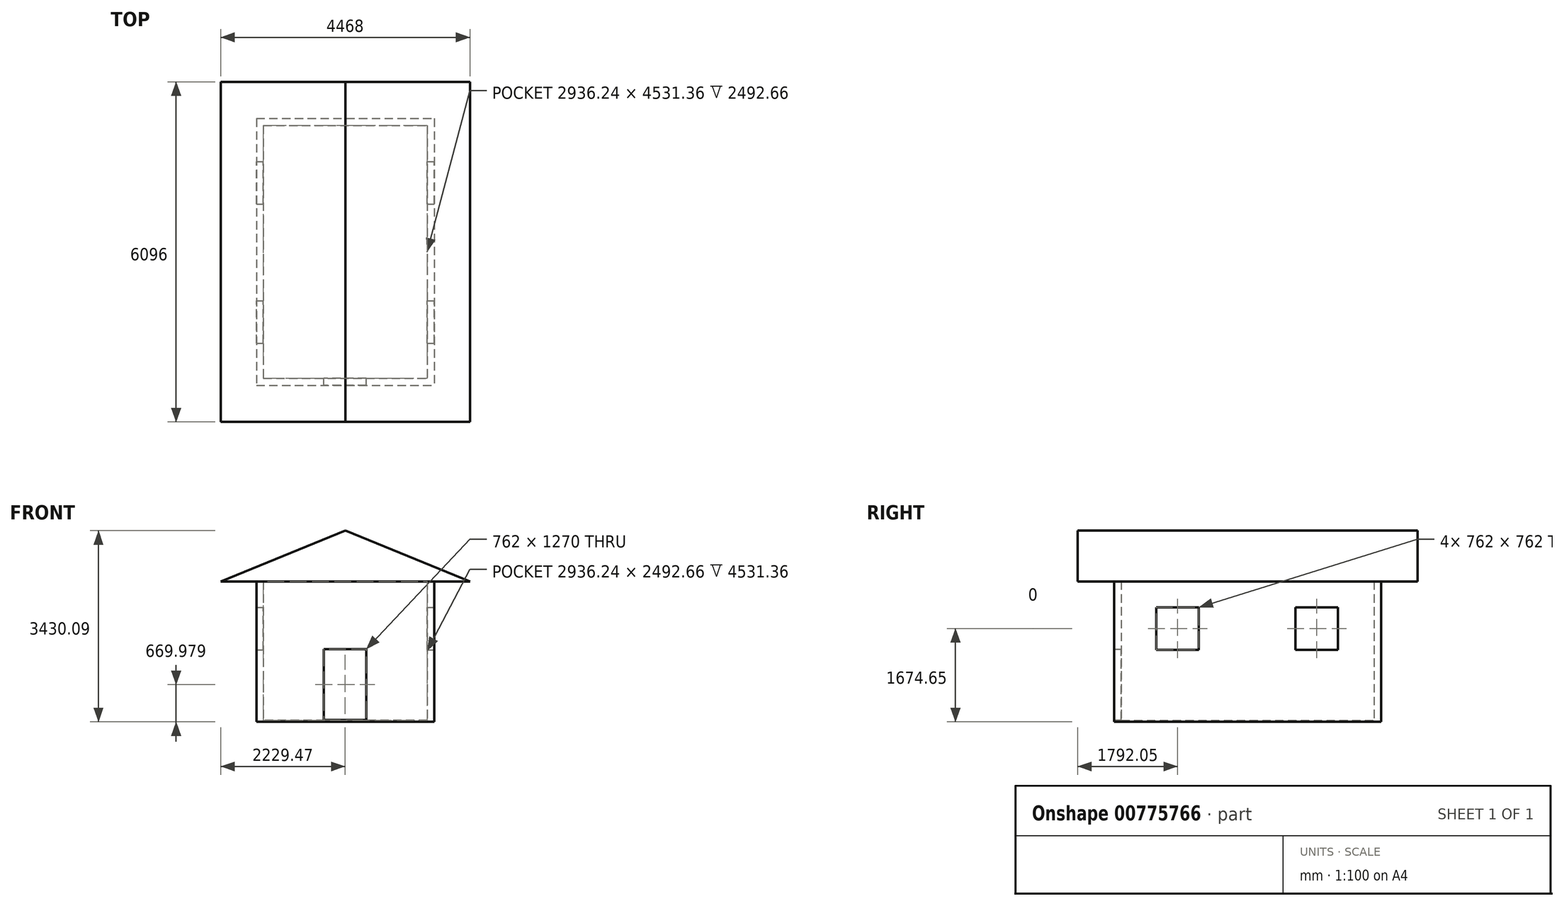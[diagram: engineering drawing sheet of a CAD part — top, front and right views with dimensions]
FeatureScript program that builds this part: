
annotation { "Feature Type Name" : "Feature", "Feature Type Description" : "" }
export const myFeature = defineFeature(function(context is Context, id is Id, definition is map)
    precondition{}
    {
        {
            var Q0;
            Q0=qCreatedBy(makeId("Top.planeOp"),FACE);
            var sketch = newSketch(context, id + "F0", { "sketchPlane" : qUnion([Q0])});
            skLineSegment(sketch, "E0.bottom", {"start": v(1595.12, -2392.68) * mm, "end": v(-1595.12, -2392.68) * mm});
            skLineSegment(sketch, "E0.top", {"start": v(1595.12, 2392.68) * mm, "end": v(-1595.12, 2392.68) * mm});
            skLineSegment(sketch, "E0.left", {"start": v(1595.12, -2392.68) * mm, "end": v(1595.12, 2392.68) * mm});
            skLineSegment(sketch, "E0.right", {"start": v(-1595.12, -2392.68) * mm, "end": v(-1595.12, 2392.68) * mm});
            skPoint(sketch, "E0.middle", {"position": v(0, 0) * mm});
            skLineSegment(sketch, "E1.bottom", {"start": v(1468.12, -2265.68) * mm, "end": v(-1468.12, -2265.68) * mm});
            skLineSegment(sketch, "E1.top", {"start": v(1468.12, 2265.68) * mm, "end": v(-1468.12, 2265.68) * mm});
            skLineSegment(sketch, "E1.left", {"start": v(1468.12, -2265.68) * mm, "end": v(1468.12, 2265.68) * mm});
            skLineSegment(sketch, "E1.right", {"start": v(-1468.12, -2265.68) * mm, "end": v(-1468.12, 2265.68) * mm});
            skSolve(sketch);
        }
        {
            var Q0;
            Q0=makeQuery(id+"F0.imprint","IMPRINT",FACE,{"disambiguationData":[TD([[makeQuery(id+"F0.imprint","IMPRINT",EDGE,{"derivedFrom":sQuery(id+"F0.wireOp",EDGE,"E0.bottom")}),-1.0]])]});
            extrude(context, id + "F1", {"entities" : qUnion([Q0]), "depth" : 2540 * mm, "offsetDistance" : 25.4 * mm});
        }
        {
            var Q0;
            Q0=makeQuery(id+"F0.imprint","IMPRINT",FACE,{"disambiguationData":[TD([[makeQuery(id+"F0.imprint","IMPRINT",EDGE,{"derivedFrom":sQuery(id+"F0.wireOp",EDGE,"E1.bottom")}),-1.0]])]});
            extrude(context, id + "F2", {"entities" : qUnion([Q0]), "operationType" : NewBodyOperationType.ADD, "depth" : 25.4 * mm, "offsetDistance" : 25.4 * mm});
        }
        {
            var Q0;
            Q0=qCreatedBy(makeId("Front.planeOp"),FACE);
            var sketch = newSketch(context, id + "F3", { "sketchPlane" : qUnion([Q0])});
            skLineSegment(sketch, "E2", {"start": v(-2234, 2518.06) * mm, "end": v(0, 3430.09) * mm});
            skLineSegment(sketch, "E3", {"start": v(0, 3430.09) * mm, "end": v(2234, 2518.06) * mm});
            skLineSegment(sketch, "E4", {"start": v(2234, 2518.06) * mm, "end": v(-2234, 2518.06) * mm});
            skSolve(sketch);
        }
        {
            var Q0;
            Q0 = qSketchRegion(id + "F3", true);
            extrude(context, id + "F4", {"entities" : qUnion([Q0]), "operationType" : NewBodyOperationType.ADD, "endBound" : BoundingType.SYMMETRIC, "depth" : 6096 * mm, "offsetDistance" : 25.4 * mm});
        }
        {
            var Q0;
            Q0=qCreatedBy(makeId("Front.planeOp"),FACE);
            var sketch = newSketch(context, id + "F5", { "sketchPlane" : qUnion([Q0])});
            skLineSegment(sketch, "E5.bottom", {"start": v(-385.53, 1304.98) * mm, "end": v(376.47, 1304.98) * mm});
            skLineSegment(sketch, "E5.top", {"start": v(-385.53, 34.98) * mm, "end": v(376.47, 34.98) * mm});
            skLineSegment(sketch, "E5.left", {"start": v(-385.53, 1304.98) * mm, "end": v(-385.53, 34.98) * mm});
            skLineSegment(sketch, "E5.right", {"start": v(376.47, 1304.98) * mm, "end": v(376.47, 34.98) * mm});
            skSolve(sketch);
        }
        {
            var Q0;
            Q0 = qSketchRegion(id + "F5", true);
            extrude(context, id + "F6", {"entities" : qUnion([Q0]), "operationType" : NewBodyOperationType.REMOVE, "oppositeDirection" : true, "depth" : -12700 * mm, "offsetDistance" : 25.4 * mm});
        }
        {
            var Q0;
            Q0=qCreatedBy(makeId("Right.planeOp"),FACE);
            var sketch = newSketch(context, id + "F7", { "sketchPlane" : qUnion([Q0])});
            skLineSegment(sketch, "E6.bottom", {"start": v(1621.9, 2055.65) * mm, "end": v(859.9, 2055.65) * mm});
            skLineSegment(sketch, "E6.top", {"start": v(1621.9, 1293.65) * mm, "end": v(859.9, 1293.65) * mm});
            skLineSegment(sketch, "E6.left", {"start": v(1621.9, 2055.65) * mm, "end": v(1621.9, 1293.65) * mm});
            skLineSegment(sketch, "E6.right", {"start": v(859.9, 2055.65) * mm, "end": v(859.9, 1293.65) * mm});
            skLineSegment(sketch, "E7.bottom", {"start": v(-874.95, 2055.65) * mm, "end": v(-1636.95, 2055.65) * mm});
            skLineSegment(sketch, "E7.top", {"start": v(-874.95, 1293.65) * mm, "end": v(-1636.95, 1293.65) * mm});
            skLineSegment(sketch, "E7.left", {"start": v(-874.95, 2055.65) * mm, "end": v(-874.95, 1293.65) * mm});
            skLineSegment(sketch, "E7.right", {"start": v(-1636.95, 2055.65) * mm, "end": v(-1636.95, 1293.65) * mm});
            skSolve(sketch);
        }
        {
            var Q0;
            Q0 = qSketchRegion(id + "F7", true);
            extrude(context, id + "F8", {"entities" : qUnion([Q0]), "operationType" : NewBodyOperationType.REMOVE, "endBound" : BoundingType.SYMMETRIC, "oppositeDirection" : true, "depth" : 7620 * mm, "offsetDistance" : 25.4 * mm});
        }
    });
